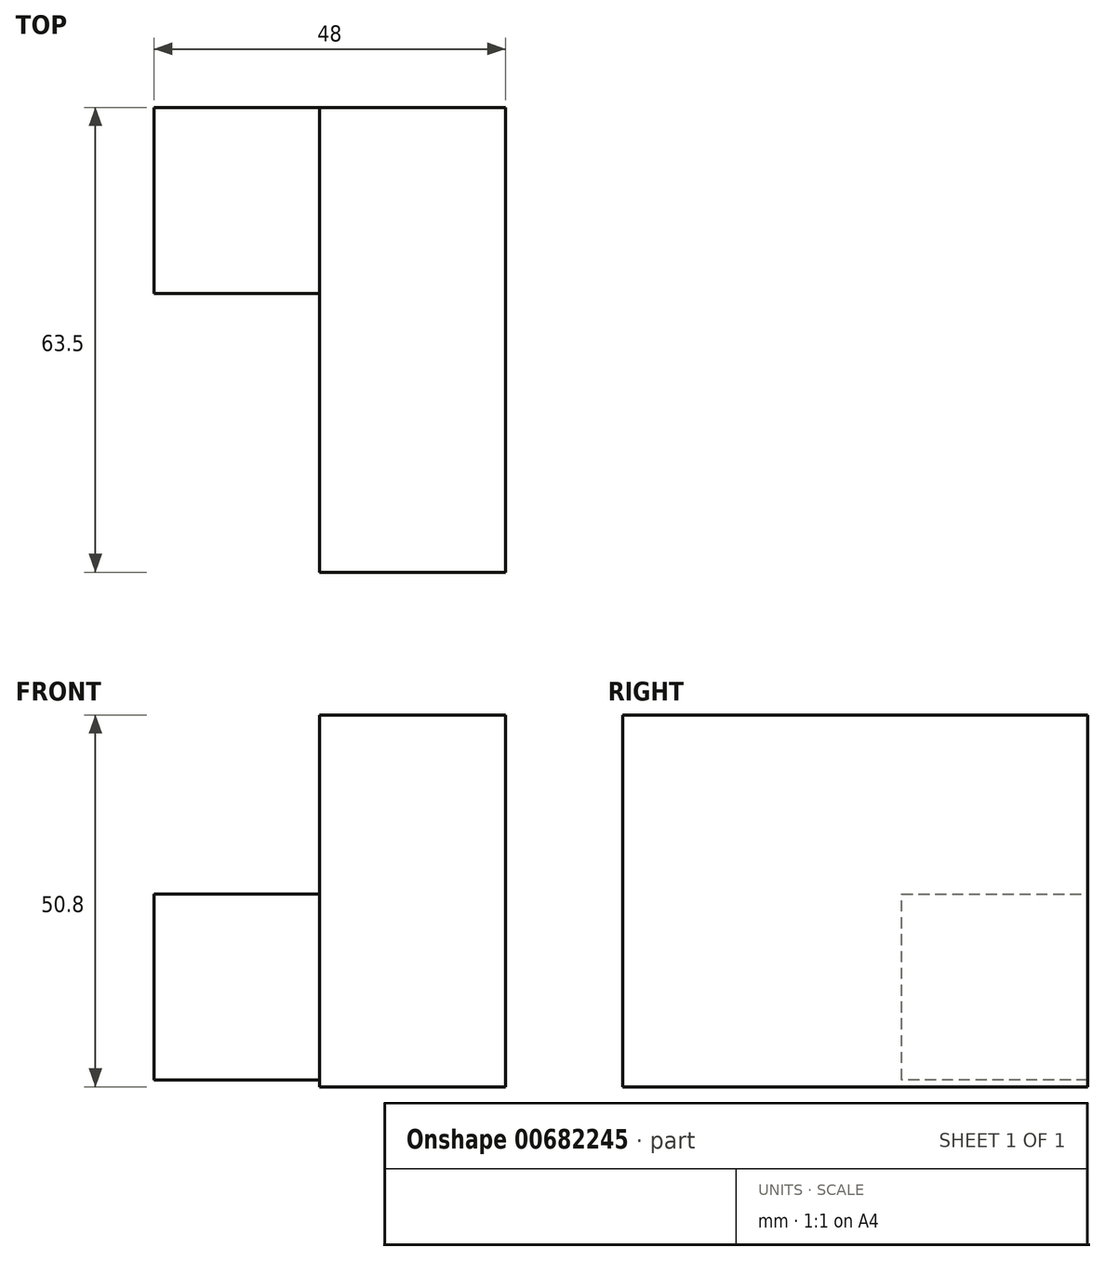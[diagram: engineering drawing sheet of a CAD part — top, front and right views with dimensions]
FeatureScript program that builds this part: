
annotation { "Feature Type Name" : "Feature", "Feature Type Description" : "" }
export const myFeature = defineFeature(function(context is Context, id is Id, definition is map)
    precondition{}
    {
        {
            var Q0;
            Q0=qCreatedBy(makeId("Front.planeOp"),FACE);
            var sketch = newSketch(context, id + "F0", { "sketchPlane" : qUnion([Q0])});
            skLineSegment(sketch, "E0", {"start": v(35.3, -32.7) * mm, "end": v(35.3, 18.1) * mm});
            skLineSegment(sketch, "E1", {"start": v(35.3, 18.1) * mm, "end": v(9.9, 18.1) * mm});
            skLineSegment(sketch, "E2", {"start": v(9.9, 18.1) * mm, "end": v(9.9, -32.7) * mm});
            skLineSegment(sketch, "E3", {"start": v(9.9, -32.7) * mm, "end": v(35.3, -32.7) * mm});
            skSolve(sketch);
        }
        {
            var Q0;
            Q0=makeQuery(id+"F0.imprint","IMPRINT",FACE,{"disambiguationData":[TD([[makeQuery(id+"F0.imprint","IMPRINT",EDGE,{"derivedFrom":sQuery(id+"F0.wireOp",EDGE,"E0")}),1.0]])]});
            extrude(context, id + "F1", {"entities" : qUnion([Q0]), "depth" : 63.5 * mm, "offsetDistance" : 25.4 * mm});
        }
        {
            var Q0;
            Q0=qCreatedBy(makeId("Right.planeOp"),FACE);
            var sketch = newSketch(context, id + "F2", { "sketchPlane" : qUnion([Q0])});
            skLineSegment(sketch, "E4", {"start": v(0, -31.75) * mm, "end": v(0, -6.35) * mm});
            skLineSegment(sketch, "E5", {"start": v(0, -6.35) * mm, "end": v(-25.4, -6.35) * mm});
            skLineSegment(sketch, "E6", {"start": v(-25.4, -6.35) * mm, "end": v(-25.4, -31.75) * mm});
            skLineSegment(sketch, "E7", {"start": v(-25.4, -31.75) * mm, "end": v(0, -31.75) * mm});
            skSolve(sketch);
        }
        {
            var Q0;
            Q0=makeQuery(id+"F2.imprint","IMPRINT",FACE,{"disambiguationData":[TD([[makeQuery(id+"F2.imprint","IMPRINT",EDGE,{"derivedFrom":sQuery(id+"F2.wireOp",EDGE,"E4")}),1.0]])]});
            extrude(context, id + "F3", {"entities" : qUnion([Q0]), "operationType" : NewBodyOperationType.ADD, "depth" : 25.15 * mm, "offsetDistance" : 25.4 * mm, "hasSecondDirection" : true, "secondDirectionOppositeDirection" : true, "secondDirectionDepth" : 12.7 * mm});
        }
    });
